# Revit family: Thorn CESAR W 140
name_source: partatom
category: Lighting Fixtures
revit_build: Autodesk Revit 2016 (Build: 20150220_1215(x64)
units: mm (PartAtom-declared; Revit-internal decimal feet)

## family parameters
Cut with Voids When Loaded = No
Host = Face
Light Source = Yes
OmniClass Number = 23.80.70.14
OmniClass Title = Luminaries for External Lighting
Part Type = Normal
Room Calculation Point = No
Round Connector Dimension = Use Diameter
Shared = No

## types (1)
- CESAR W 140
    Apparent Load = 16 VA
    Assembly Code = D5020200
    Body = ZG_Plastic_Black
    Color Filter = 16777215
    Default Elevation = 0 mm  [stored 0 ft]
    Description = Wall mounted LED luminaires
    Dimming Lamp Color Temperature Shift = <None>
    Emit Shape Visible in Rendering = No
    Emit from Circle Diameter = 100 mm  [stored 0.328084 ft]
    Height = 315 mm  [stored 1.03346 ft]
    Lamp = LED
    Length = 140 mm  [stored 0.459318 ft]
    Manufacturer = Thorn Lighting
    Model = 96632342
    Photometric Web File = 96632342_(STD).IES
    Reflector = ZG_Cover_Self_llumination_Opaque
    Tilt Angle = 90.00°
    URL = www.thornlighting.com/96632342
    Voltage = 230 V
    Width = 210 mm  [stored 0.688976 ft]

note: [stored X ft] marks values corroborated as IEEE doubles in the binary element streams (Revit-internal decimal feet)

## geometry (parser evidence)
native form markers: Sweep x3
no freeform markers — native parametric forms only
